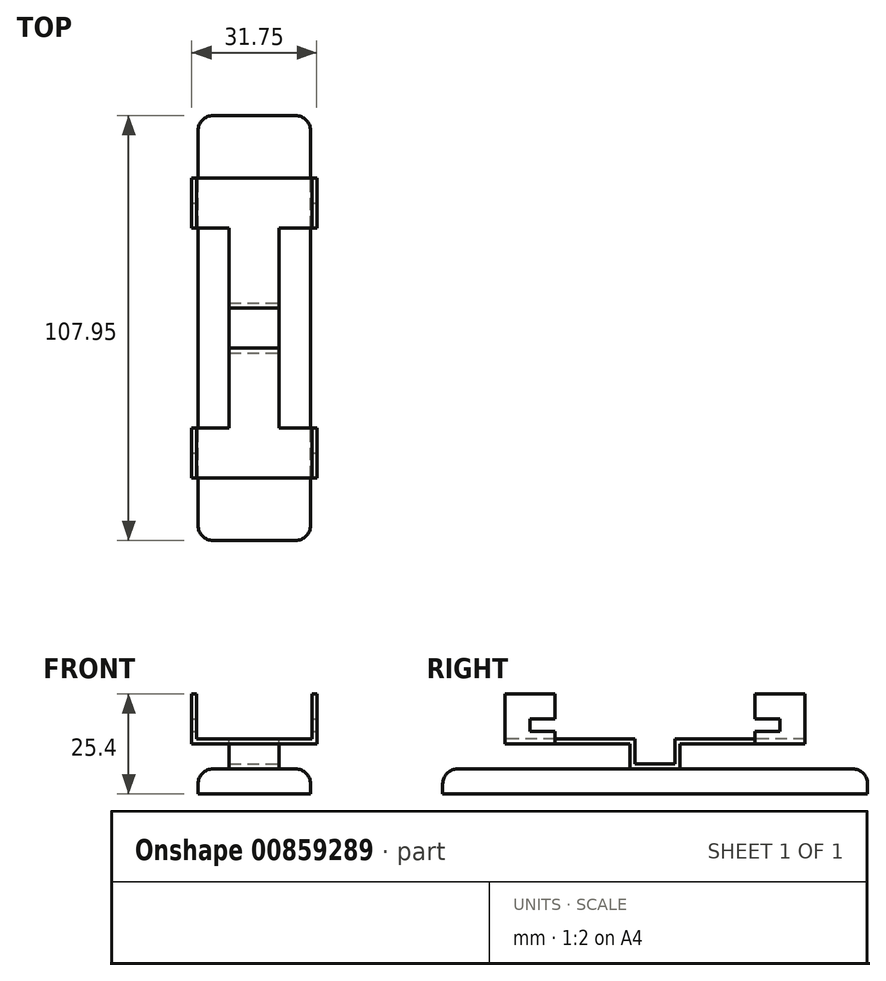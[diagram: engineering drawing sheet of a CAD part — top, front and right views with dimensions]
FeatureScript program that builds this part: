
annotation { "Feature Type Name" : "Feature", "Feature Type Description" : "" }
export const myFeature = defineFeature(function(context is Context, id is Id, definition is map)
    precondition{}
    {
        {
            var Q0;
            Q0=qCreatedBy(makeId("Top.planeOp"),FACE);
            var sketch = newSketch(context, id + "F0", { "sketchPlane" : qUnion([Q0])});
            skLineSegment(sketch, "E0.bottom", {"start": v(0, 0) * mm, "end": v(28.58, 0) * mm});
            skLineSegment(sketch, "E0.top", {"start": v(0, 107.95) * mm, "end": v(28.57, 107.95) * mm});
            skLineSegment(sketch, "E0.left", {"start": v(0, 0) * mm, "end": v(0, 107.95) * mm});
            skLineSegment(sketch, "E0.right", {"start": v(28.58, 0) * mm, "end": v(28.57, 107.95) * mm});
            skSolve(sketch);
        }
        {
            var Q0;
            Q0=makeQuery(id+"F0.imprint","IMPRINT",FACE,{"disambiguationData":[TD([[makeQuery(id+"F0.imprint","IMPRINT",EDGE,{"derivedFrom":sQuery(id+"F0.wireOp",EDGE,"E0.bottom")}),1.0]])]});
            extrude(context, id + "F1", {"entities" : qUnion([Q0]), "depth" : 6.35 * mm, "offsetDistance" : 25.4 * mm});
        }
        {
            var Q0;
            Q0=makeQuery(id+"F1.opExtrude","SWEPT_EDGE",EDGE,{"disambiguationData":[OSD([sQuery(id+"F0.wireOp",EDGE,"E0.bottom"),sQuery(id+"F0.wireOp",EDGE,"E0.right")])]});
            var Q1;
            Q1=makeQuery(id+"F1.opExtrude","SWEPT_EDGE",EDGE,{"disambiguationData":[OSD([sQuery(id+"F0.wireOp",EDGE,"E0.bottom"),sQuery(id+"F0.wireOp",EDGE,"E0.left")])]});
            var Q2;
            Q2=makeQuery(id+"F1.opExtrude","SWEPT_EDGE",EDGE,{"disambiguationData":[OSD([sQuery(id+"F0.wireOp",EDGE,"E0.top"),sQuery(id+"F0.wireOp",EDGE,"E0.right")])]});
            var Q3;
            Q3=makeQuery(id+"F1.opExtrude","SWEPT_EDGE",EDGE,{"disambiguationData":[OSD([sQuery(id+"F0.wireOp",EDGE,"E0.top"),sQuery(id+"F0.wireOp",EDGE,"E0.left")])]});
            var Q4;
            Q4=makeQuery(id+"F1.opExtrude","CAP_FACE",FACE,{"disambiguationData":[OSD([sQuery(id+"F0.wireOp",EDGE,"E0.bottom"),sQuery(id+"F0.wireOp",EDGE,"E0.top"),sQuery(id+"F0.wireOp",EDGE,"E0.left"),sQuery(id+"F0.wireOp",EDGE,"E0.right")])],"isStart":false});
            fillet(context, id + "F2", {"entities" : qUnion([Q0, Q1, Q2, Q3, Q4]), "radius" : 3.8 * mm, "tangentPropagation" : true, "allowEdgeOverflow" : false});
        }
        {
            var Q0;
            Q0=makeQuery(id+"F1.opExtrude","CAP_EDGE",EDGE,{"disambiguationData":[OSD([sQuery(id+"F0.wireOp",EDGE,"E0.bottom")])],"isStart":true});
            cPoint(context, id + "F3", {"entities" : qUnion([Q0]), "parameter" : 0.5});
        }
        {
            var Q0;
            {var subQ0=sQuery(id+"F0.wireOp",EDGE,"E0.bottom");Q0=makeQuery(id+"F2.opFillet","BLEND_EDGE",EDGE,{"blendedFrom":[makeQuery(id+"F1.opExtrude","CAP_EDGE",EDGE,{"disambiguationData":[OSD([subQ0])],"isStart":false}),makeQuery(id+"F1.opExtrude","SWEPT_FACE",FACE,{"disambiguationData":[OSD([subQ0])]})],"blendedInto":[makeQuery(id+"F1.opExtrude","SWEPT_FACE",FACE,{"disambiguationData":[OSD([subQ0])]})]});}
            cPoint(context, id + "F4", {"entities" : qUnion([Q0]), "parameter" : 0.5});
        }
        {
            var Q0;
            {var subQ0=sQuery(id+"F0.wireOp",EDGE,"E0.bottom");Q0=makeQuery(id+"F2.opFillet","BLEND_EDGE",EDGE,{"blendedFrom":[makeQuery(id+"F1.opExtrude","CAP_EDGE",EDGE,{"disambiguationData":[OSD([subQ0])],"isStart":false}),makeQuery(id+"F1.opExtrude","CAP_FACE",FACE,{"disambiguationData":[OSD([subQ0,sQuery(id+"F0.wireOp",EDGE,"E0.top"),sQuery(id+"F0.wireOp",EDGE,"E0.left"),sQuery(id+"F0.wireOp",EDGE,"E0.right")])],"isStart":false})],"blendedInto":[makeQuery(id+"F1.opExtrude","CAP_FACE",FACE,{"disambiguationData":[OSD([subQ0,sQuery(id+"F0.wireOp",EDGE,"E0.top"),sQuery(id+"F0.wireOp",EDGE,"E0.left"),sQuery(id+"F0.wireOp",EDGE,"E0.right")])],"isStart":false})]});}
            cPoint(context, id + "F5", {"entities" : qUnion([Q0]), "parameter" : 0.5});
        }
        {
            var Q0;
            Q0 = qCreatedBy(id + "F3" ,VERTEX);
            var Q1;
            Q1 = qCreatedBy(id + "F4" ,VERTEX);
            var Q2;
            Q2 = qCreatedBy(id + "F5" ,VERTEX);
            cPlane(context, id + "F6", {"entities" : qUnion([Q0, Q1, Q2]), "cplaneType" : CPlaneType.THREE_POINT, "offset" : 25.4 * mm, "width" : 152.4 * mm, "height" : 152.4 * mm});
        }
        {
            var Q0;
            Q0=qCreatedBy(id+"F6.planeOp",FACE);
            var sketch = newSketch(context, id + "F7", { "sketchPlane" : qUnion([Q0])});
            skLineSegment(sketch, "E1.bottom", {"start": v(15.87, 25.4) * mm, "end": v(28.57, 25.4) * mm});
            skLineSegment(sketch, "E1.top", {"start": v(15.87, 12.7) * mm, "end": v(47.62, 12.7) * mm});
            skLineSegment(sketch, "E1.left", {"start": v(15.87, 25.4) * mm, "end": v(15.87, 12.7) * mm});
            skLineSegment(sketch, "E1.right", {"start": v(92.07, 25.4) * mm, "end": v(92.07, 12.7) * mm});
            skPoint(sketch, "E2.0", {"position": v(53.97, 6.35) * mm});
            skLineSegment(sketch, "E3", {"start": v(53.97, 6.35) * mm, "end": v(53.97, 12.7) * mm, "construction": true});
            skLineSegment(sketch, "E4.top", {"start": v(28.57, 13.97) * mm, "end": v(48.9, 13.97) * mm});
            skLineSegment(sketch, "E4.left", {"start": v(28.57, 25.4) * mm, "end": v(28.57, 19.05) * mm});
            skLineSegment(sketch, "E4.right", {"start": v(79.37, 25.4) * mm, "end": v(79.37, 19.05) * mm});
            skLineSegment(sketch, "E5.trimOffspring", {"start": v(79.37, 25.4) * mm, "end": v(92.07, 25.4) * mm});
            skLineSegment(sketch, "E6", {"start": v(53.97, 6.35) * mm, "end": v(47.62, 6.35) * mm});
            skLineSegment(sketch, "E7", {"start": v(47.62, 6.35) * mm, "end": v(47.62, 12.7) * mm});
            skLineSegment(sketch, "E8", {"start": v(53.97, 6.35) * mm, "end": v(60.32, 6.35) * mm});
            skLineSegment(sketch, "E9", {"start": v(60.32, 6.35) * mm, "end": v(60.32, 12.7) * mm});
            skLineSegment(sketch, "E10.trimOffspring", {"start": v(60.32, 12.7) * mm, "end": v(92.07, 12.7) * mm});
            skLineSegment(sketch, "E11.bottom", {"start": v(28.57, 15.87) * mm, "end": v(22.22, 15.87) * mm});
            skLineSegment(sketch, "E11.top", {"start": v(28.57, 19.05) * mm, "end": v(22.22, 19.05) * mm});
            skLineSegment(sketch, "E11.right", {"start": v(22.22, 15.87) * mm, "end": v(22.22, 19.05) * mm});
            skLineSegment(sketch, "E12.bottom", {"start": v(79.37, 15.88) * mm, "end": v(85.72, 15.88) * mm});
            skLineSegment(sketch, "E12.top", {"start": v(79.37, 19.05) * mm, "end": v(85.72, 19.05) * mm});
            skLineSegment(sketch, "E12.right", {"start": v(85.72, 15.88) * mm, "end": v(85.72, 19.05) * mm});
            skLineSegment(sketch, "E13.trimOffspring", {"start": v(28.57, 15.87) * mm, "end": v(28.57, 13.97) * mm});
            skLineSegment(sketch, "E14.trimOffspring", {"start": v(79.37, 15.88) * mm, "end": v(79.37, 13.97) * mm});
            skLineSegment(sketch, "E15.top", {"start": v(48.9, 7.62) * mm, "end": v(59.05, 7.62) * mm});
            skLineSegment(sketch, "E15.left", {"start": v(48.9, 13.97) * mm, "end": v(48.9, 7.62) * mm});
            skLineSegment(sketch, "E15.right", {"start": v(59.05, 13.97) * mm, "end": v(59.05, 7.62) * mm});
            skLineSegment(sketch, "E16.trimOffspring", {"start": v(59.05, 13.97) * mm, "end": v(79.37, 13.97) * mm});
            skSolve(sketch);
        }
        {
            var Q0;
            Q0=makeQuery(id+"F7.imprint","IMPRINT",FACE,{"disambiguationData":[TD([[makeQuery(id+"F7.imprint","IMPRINT",EDGE,{"derivedFrom":sQuery(id+"F7.wireOp",EDGE,"E1.bottom")}),-1.0]])]});
            extrude(context, id + "F8", {"entities" : qUnion([Q0]), "operationType" : NewBodyOperationType.ADD, "oppositeDirection" : true, "depth" : 15.88 * mm, "offsetDistance" : 25.4 * mm, "hasSecondDirection" : true, "secondDirectionOppositeDirection" : false, "secondDirectionDepth" : 15.88 * mm});
        }
        {
            var Q0;
            Q0=makeQuery(id+"F8.opExtrude","SWEPT_FACE",FACE,{"disambiguationData":[OSD([sQuery(id+"F7.wireOp",EDGE,"E1.left")])]});
            var sketch = newSketch(context, id + "F9", { "sketchPlane" : qUnion([Q0])});
            skLineSegment(sketch, "E17.bottom", {"start": v(-0.32, 25.4) * mm, "end": v(28.9, 25.4) * mm});
            skLineSegment(sketch, "E17.top", {"start": v(-0.32, 13.97) * mm, "end": v(28.9, 13.97) * mm});
            skLineSegment(sketch, "E17.left", {"start": v(-0.32, 25.4) * mm, "end": v(-0.32, 13.97) * mm});
            skLineSegment(sketch, "E17.right", {"start": v(28.9, 25.4) * mm, "end": v(28.9, 13.97) * mm});
            skPoint(sketch, "E18.0", {"position": v(-1.59, 6.35) * mm});
            skPoint(sketch, "E19.0", {"position": v(30.16, 6.35) * mm});
            skLineSegment(sketch, "E20.bottom", {"start": v(-1.59, 6.35) * mm, "end": v(7.94, 6.35) * mm});
            skLineSegment(sketch, "E20.top", {"start": v(-1.59, 12.7) * mm, "end": v(7.94, 12.7) * mm});
            skLineSegment(sketch, "E20.left", {"start": v(-1.59, 6.35) * mm, "end": v(-1.59, 12.7) * mm});
            skLineSegment(sketch, "E20.right", {"start": v(7.94, 6.35) * mm, "end": v(7.94, 12.7) * mm});
            skLineSegment(sketch, "E21.bottom", {"start": v(30.16, 6.35) * mm, "end": v(20.64, 6.35) * mm});
            skLineSegment(sketch, "E21.top", {"start": v(30.16, 12.7) * mm, "end": v(20.64, 12.7) * mm});
            skLineSegment(sketch, "E21.left", {"start": v(30.16, 6.35) * mm, "end": v(30.16, 12.7) * mm});
            skLineSegment(sketch, "E21.right", {"start": v(20.64, 6.35) * mm, "end": v(20.64, 12.7) * mm});
            skSolve(sketch);
        }
        {
            var Q0;
            Q0=makeQuery(id+"F9.imprint","IMPRINT",FACE,{"disambiguationData":[TD([[makeQuery(id+"F9.imprint","IMPRINT",EDGE,{"derivedFrom":sQuery(id+"F9.wireOp",EDGE,"E20.bottom")}),1.0]])]});
            var Q1;
            Q1=makeQuery(id+"F9.imprint","IMPRINT",FACE,{"disambiguationData":[TD([[makeQuery(id+"F9.imprint","IMPRINT",EDGE,{"derivedFrom":sQuery(id+"F9.wireOp",EDGE,"E17.bottom")}),-1.0]])]});
            var Q2;
            Q2=makeQuery(id+"F9.imprint","IMPRINT",FACE,{"disambiguationData":[TD([[makeQuery(id+"F9.imprint","IMPRINT",EDGE,{"derivedFrom":sQuery(id+"F9.wireOp",EDGE,"E21.bottom")}),-1.0]])]});
            extrude(context, id + "F10", {"entities" : qUnion([Q0, Q1, Q2]), "operationType" : NewBodyOperationType.REMOVE, "endBound" : BoundingType.THROUGH_ALL, "oppositeDirection" : true, "depth" : 25.4 * mm, "offsetDistance" : 25.4 * mm});
        }
        {
            var Q0;
            Q0=makeQuery(id+"F10.boolean.opBoolean","MERGE",FACE,{"derivedFrom":[makeQuery(id+"F8.opExtrude","SWEPT_FACE",FACE,{"disambiguationData":[OSD([sQuery(id+"F7.wireOp",EDGE,"E16.trimOffspring")])]}),makeQuery(id+"F10.opExtrude","SWEPT_FACE",FACE,{"disambiguationData":[OSD([sQuery(id+"F9.wireOp",EDGE,"E17.top")])]})]});
            var sketch = newSketch(context, id + "F11", { "sketchPlane" : qUnion([Q0])});
            skLineSegment(sketch, "E22.bottom", {"start": v(-1.59, 79.37) * mm, "end": v(7.94, 79.37) * mm});
            skLineSegment(sketch, "E22.top", {"start": v(-1.59, 28.57) * mm, "end": v(7.94, 28.57) * mm});
            skLineSegment(sketch, "E22.left", {"start": v(-1.59, 79.37) * mm, "end": v(-1.59, 28.57) * mm});
            skLineSegment(sketch, "E22.right", {"start": v(7.94, 79.37) * mm, "end": v(7.94, 28.57) * mm});
            skLineSegment(sketch, "E23.bottom", {"start": v(30.16, 79.38) * mm, "end": v(20.64, 79.38) * mm});
            skLineSegment(sketch, "E23.top", {"start": v(30.16, 28.57) * mm, "end": v(20.64, 28.57) * mm});
            skLineSegment(sketch, "E23.left", {"start": v(30.16, 79.38) * mm, "end": v(30.16, 28.57) * mm});
            skLineSegment(sketch, "E23.right", {"start": v(20.64, 79.37) * mm, "end": v(20.64, 28.57) * mm});
            skPoint(sketch, "E24.0", {"position": v(-1.59, 28.57) * mm});
            skLineSegment(sketch, "E25.0", {"start": v(7.94, 59.06) * mm, "end": v(7.94, 48.9) * mm});
            skLineSegment(sketch, "E26.0", {"start": v(20.64, 59.06) * mm, "end": v(20.64, 48.9) * mm});
            skSolve(sketch);
        }
        {
            var Q0;
            {var subQ4=sQuery(id+"F11.wireOp",EDGE,"E22.top");Q0=makeQuery(id+"F11.imprint","IMPRINT",FACE,{"disambiguationData":[TD([[makeQuery(id+"F11.imprint","IMPRINT",EDGE,{"derivedFrom":subQ4}),1.0]])]});}
            var Q1;
            {var subQ0=sQuery(id+"F11.wireOp",EDGE,"E22.left");var subQ1=sQuery(id+"F11.wireOp",EDGE,"E22.bottom");var subQ2=makeQuery(id+"F11.imprint","INTERSECT",VERTEX,{"derivedFrom":[subQ1,subQ0]});Q1=makeQuery(id+"F11.imprint","IMPRINT",FACE,{"disambiguationData":[TD([[makeQuery(id+"F11.imprint","IMPRINT",EDGE,{"disambiguationData":[TD([[subQ2,1.0]])],"derivedFrom":subQ0}),-1.0]])]});}
            var Q2;
            {var subQ1=sQuery(id+"F11.wireOp",EDGE,"E23.top");Q2=makeQuery(id+"F11.imprint","IMPRINT",FACE,{"disambiguationData":[TD([[makeQuery(id+"F11.imprint","IMPRINT",EDGE,{"derivedFrom":subQ1}),-1.0]])]});}
            var Q3;
            {var subQ0=sQuery(id+"F11.wireOp",EDGE,"E23.left");var subQ1=sQuery(id+"F11.wireOp",EDGE,"E23.bottom");var subQ2=makeQuery(id+"F11.imprint","INTERSECT",VERTEX,{"derivedFrom":[subQ1,subQ0]});Q3=makeQuery(id+"F11.imprint","IMPRINT",FACE,{"disambiguationData":[TD([[makeQuery(id+"F11.imprint","IMPRINT",EDGE,{"disambiguationData":[TD([[subQ2,1.0]])],"derivedFrom":subQ0}),1.0]])]});}
            var Q4;
            {var subQ0=sQuery(id+"F0.wireOp",EDGE,"E0.left");var subQ2=sQuery(id+"F0.wireOp",EDGE,"E0.top");var subQ4=sQuery(id+"F0.wireOp",EDGE,"E0.right");var subQ6=sQuery(id+"F0.wireOp",EDGE,"E0.bottom");var subQ7=makeQuery(id+"F1.opExtrude","CAP_FACE",FACE,{"disambiguationData":[OSD([subQ6,subQ2,subQ0,subQ4])],"isStart":false});Q4=makeQuery(id+"F10.boolean.opBoolean","MERGE",FACE,{"derivedFrom":[makeQuery(id+"F8.boolean.opBoolean","SPLIT",FACE,{"disambiguationData":[TD([makeQuery(id+"F2.opFillet","BLEND_FACE",FACE,{"disambiguationData":[OSD([subQ6])]})])],"derivedFrom":subQ7}),makeQuery(id+"F8.boolean.opBoolean","SPLIT",FACE,{"disambiguationData":[TD([makeQuery(id+"F2.opFillet","BLEND_FACE",FACE,{"disambiguationData":[OSD([subQ2])]})])],"derivedFrom":subQ7}),makeQuery(id+"F10.opExtrude","SWEPT_FACE",FACE,{"disambiguationData":[OSD([sQuery(id+"F9.wireOp",EDGE,"E20.bottom")])]}),makeQuery(id+"F10.opExtrude","SWEPT_FACE",FACE,{"disambiguationData":[OSD([sQuery(id+"F9.wireOp",EDGE,"E21.bottom")])]})]});}
            extrude(context, id + "F12", {"entities" : qUnion([Q0, Q1, Q2, Q3]), "operationType" : NewBodyOperationType.REMOVE, "endBound" : BoundingType.UP_TO_SURFACE, "oppositeDirection" : true, "depth" : 25.4 * mm, "endBoundEntityFace" : qUnion([Q4]), "offsetDistance" : 25.4 * mm});
        }
    });
